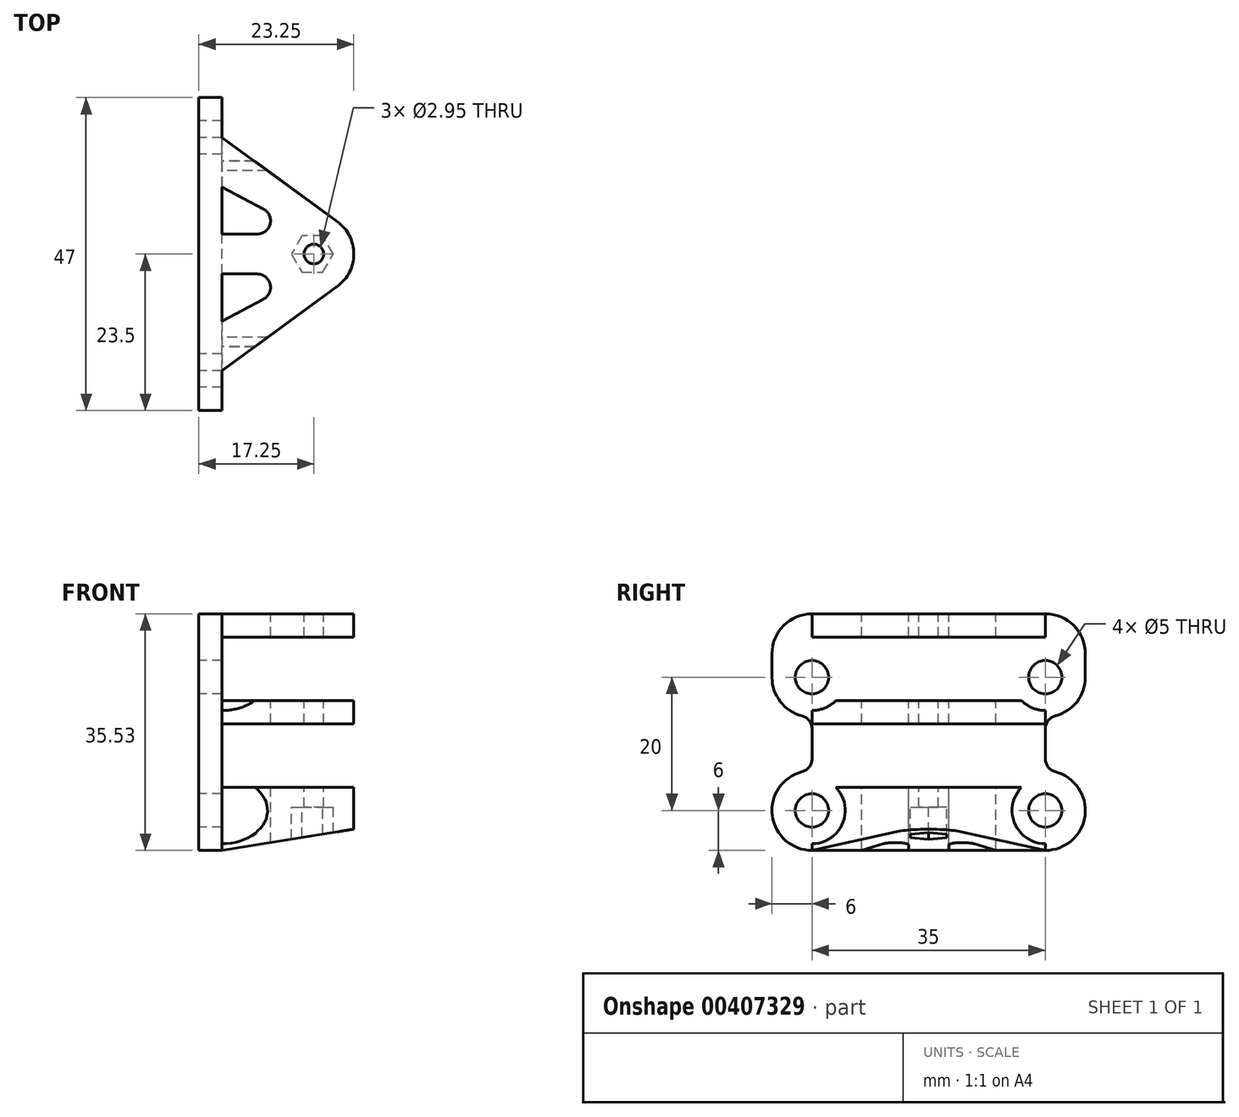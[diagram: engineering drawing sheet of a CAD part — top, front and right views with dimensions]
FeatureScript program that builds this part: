
annotation { "Feature Type Name" : "Feature", "Feature Type Description" : "" }
export const myFeature = defineFeature(function(context is Context, id is Id, definition is map)
    precondition{}
    {
        {
            var Q0;
            Q0=qCreatedBy(makeId("Right.planeOp"),FACE);
            var sketch = newSketch(context, id + "F0", { "sketchPlane" : qUnion([Q0])});
            skLineSegment(sketch, "E0", {"start": v(0, 0) * mm, "end": v(136.08, 0) * mm, "construction": true});
            skLineSegment(sketch, "E1", {"start": v(0, -20) * mm, "end": v(136.08, -20) * mm, "construction": true});
            skLineSegment(sketch, "E2.MirrorCS", {"start": v(0, 20) * mm, "end": v(136.08, 20) * mm, "construction": true});
            skLineSegment(sketch, "E3", {"start": v(0, 20) * mm, "end": v(0, -20) * mm, "construction": true});
            skLineSegment(sketch, "E4", {"start": v(0, -10) * mm, "end": v(136.08, -10) * mm, "construction": true});
            skLineSegment(sketch, "E5.MirrorCS", {"start": v(0, 10) * mm, "end": v(136.08, 10) * mm, "construction": true});
            skLineSegment(sketch, "E6", {"start": v(0, -13.1) * mm, "end": v(136.08, -13.1) * mm, "construction": true});
            skLineSegment(sketch, "E7.MirrorCS", {"start": v(0, -6.9) * mm, "end": v(136.08, -6.9) * mm, "construction": true});
            skLineSegment(sketch, "E8.MirrorCS", {"start": v(0, 6.9) * mm, "end": v(136.08, 6.9) * mm, "construction": true});
            skLineSegment(sketch, "E9.MirrorCS", {"start": v(0, 13.1) * mm, "end": v(136.08, 13.1) * mm, "construction": true});
            skCircle(sketch, "E10", {"center": v(78.97, -10) * mm, "radius": 8 * mm});
            skCircle(sketch, "E11", {"center": v(101.3, 2.1) * mm, "radius": 8 * mm});
            skCircle(sketch, "E12.0", {"center": v(78.97, -10) * mm, "radius": 9.4 * mm});
            skCircle(sketch, "E13.0", {"center": v(101.3, 2.1) * mm, "radius": 9.4 * mm});
            skLineSegment(sketch, "E14", {"start": v(78.97, -1.75) * mm, "end": v(13.68, -1.75) * mm, "construction": true});
            skArc(sketch, "E15", {"start": v(87.21, -10.39) * mm, "mid": v(84.94, -4.3) * mm, "end": v(78.97, -1.75) * mm, "construction": true});
            skLineSegment(sketch, "E16", {"start": v(101.3, 11.25) * mm, "end": v(11.45, 11.25) * mm, "construction": true});
            skArc(sketch, "E17", {"start": v(101.3, 11.25) * mm, "mid": v(108.42, 7.84) * mm, "end": v(110.23, 0.16) * mm, "construction": true});
            skLineSegment(sketch, "E18", {"start": v(22, 11.25) * mm, "end": v(22, -1.75) * mm, "construction": true});
            skLineSegment(sketch, "E19", {"start": v(29.5, -1.75) * mm, "end": v(29.5, 11.25) * mm, "construction": true});
            skLineSegment(sketch, "E20", {"start": v(25.75, -1.75) * mm, "end": v(25.75, 11.25) * mm, "construction": true});
            skLineSegment(sketch, "E21", {"start": v(26, -4.75) * mm, "end": v(26, 1.25) * mm, "construction": true});
            skLineSegment(sketch, "E22", {"start": v(26, 1.25) * mm, "end": v(36, 1.25) * mm, "construction": true});
            skLineSegment(sketch, "E23", {"start": v(36, 1.25) * mm, "end": v(36, -4.75) * mm, "construction": true});
            skLineSegment(sketch, "E24", {"start": v(36, -4.75) * mm, "end": v(26, -4.75) * mm, "construction": true});
            skLineSegment(sketch, "E25.bottom", {"start": v(26, 14.25) * mm, "end": v(36, 14.25) * mm, "construction": true});
            skLineSegment(sketch, "E25.top", {"start": v(26, 8.25) * mm, "end": v(36, 8.25) * mm, "construction": true});
            skLineSegment(sketch, "E25.left", {"start": v(26, 14.25) * mm, "end": v(26, 8.25) * mm, "construction": true});
            skLineSegment(sketch, "E25.right", {"start": v(36, 14.25) * mm, "end": v(36, 8.25) * mm, "construction": true});
            skLineSegment(sketch, "E26.bottom", {"start": v(54.5, -16) * mm, "end": v(7.5, -16) * mm});
            skLineSegment(sketch, "E26.top", {"start": v(54.5, 19.52) * mm, "end": v(7.5, 19.52) * mm});
            skLineSegment(sketch, "E26.left", {"start": v(54.5, -16) * mm, "end": v(54.5, 19.52) * mm});
            skLineSegment(sketch, "E26.right", {"start": v(7.5, -16) * mm, "end": v(7.5, 19.52) * mm});
            skCircle(sketch, "E27", {"center": v(48.5, -10) * mm, "radius": 2.5 * mm});
            skCircle(sketch, "E28", {"center": v(13.5, -10) * mm, "radius": 2.5 * mm});
            skCircle(sketch, "E29", {"center": v(13.5, -10) * mm, "radius": 5 * mm});
            skCircle(sketch, "E30", {"center": v(48.5, -10) * mm, "radius": 5 * mm});
            skCircle(sketch, "E31", {"center": v(48.5, 10) * mm, "radius": 2.5 * mm});
            skCircle(sketch, "E32", {"center": v(48.5, 10) * mm, "radius": 5 * mm});
            skCircle(sketch, "E33", {"center": v(13.5, 10) * mm, "radius": 2.5 * mm});
            skCircle(sketch, "E34", {"center": v(13.5, 10) * mm, "radius": 5 * mm});
            skLineSegment(sketch, "E35", {"start": v(48.5, -10) * mm, "end": v(48.5, 10) * mm, "construction": true});
            skLineSegment(sketch, "E36", {"start": v(13.5, -10) * mm, "end": v(13.5, 10) * mm, "construction": true});
            skLineSegment(sketch, "E37", {"start": v(34.42, 8.25) * mm, "end": v(34.42, 6.47) * mm, "construction": true});
            skLineSegment(sketch, "E38", {"start": v(34.42, 6.47) * mm, "end": v(27.58, 6.47) * mm});
            skLineSegment(sketch, "E39", {"start": v(27.58, 6.47) * mm, "end": v(27.58, 8.25) * mm, "construction": true});
            skLineSegment(sketch, "E40", {"start": v(31, 20.34) * mm, "end": v(31, -14.66) * mm, "construction": true});
            skLineSegment(sketch, "E41", {"start": v(34.42, 14.25) * mm, "end": v(34.42, 16.02) * mm, "construction": true});
            skLineSegment(sketch, "E42", {"start": v(34.42, 16.02) * mm, "end": v(27.58, 16.02) * mm, "construction": true});
            skLineSegment(sketch, "E43", {"start": v(27.58, 16.02) * mm, "end": v(27.58, 14.25) * mm, "construction": true});
            skLineSegment(sketch, "E44", {"start": v(34.42, -4.75) * mm, "end": v(34.42, -6.53) * mm, "construction": true});
            skLineSegment(sketch, "E45", {"start": v(34.42, -6.53) * mm, "end": v(27.58, -6.53) * mm, "construction": true});
            skLineSegment(sketch, "E46", {"start": v(27.58, -6.53) * mm, "end": v(27.58, -4.75) * mm, "construction": true});
            skLineSegment(sketch, "E47", {"start": v(34.42, 1.25) * mm, "end": v(34.42, 3.02) * mm, "construction": true});
            skLineSegment(sketch, "E48", {"start": v(34.42, 3.02) * mm, "end": v(27.58, 3.02) * mm, "construction": true});
            skLineSegment(sketch, "E49", {"start": v(27.58, 3.02) * mm, "end": v(27.58, 1.25) * mm, "construction": true});
            skLineSegment(sketch, "E50.bottom", {"start": v(48.5, 16.02) * mm, "end": v(13.5, 16.02) * mm});
            skLineSegment(sketch, "E50.top", {"start": v(48.5, 19.52) * mm, "end": v(13.5, 19.52) * mm});
            skLineSegment(sketch, "E50.left", {"start": v(48.5, 16.02) * mm, "end": v(48.5, 19.52) * mm});
            skLineSegment(sketch, "E50.right", {"start": v(13.5, 16.02) * mm, "end": v(13.5, 19.52) * mm});
            skLineSegment(sketch, "E51.bottom", {"start": v(48.5, 3.02) * mm, "end": v(13.5, 3.02) * mm});
            skLineSegment(sketch, "E51.top", {"start": v(48.5, 6.47) * mm, "end": v(13.5, 6.47) * mm});
            skLineSegment(sketch, "E51.left", {"start": v(48.5, 3.02) * mm, "end": v(48.5, 6.47) * mm});
            skLineSegment(sketch, "E51.right", {"start": v(13.5, 3.02) * mm, "end": v(13.5, 6.47) * mm});
            skLineSegment(sketch, "E52.bottom", {"start": v(48.5, -14.03) * mm, "end": v(13.5, -14.03) * mm});
            skLineSegment(sketch, "E52.top", {"start": v(48.5, -6.53) * mm, "end": v(13.5, -6.53) * mm});
            skLineSegment(sketch, "E52.left", {"start": v(48.5, -14.03) * mm, "end": v(48.5, -6.53) * mm});
            skLineSegment(sketch, "E52.right", {"start": v(13.5, -14.03) * mm, "end": v(13.5, -6.53) * mm});
            skLineSegment(sketch, "E53", {"start": v(32.45, 20.34) * mm, "end": v(32.45, -14.66) * mm, "construction": true});
            skLineSegment(sketch, "E54", {"start": v(32.45, -14.66) * mm, "end": v(29.55, -14.66) * mm, "construction": true});
            skLineSegment(sketch, "E55", {"start": v(29.55, -14.66) * mm, "end": v(29.55, 20.34) * mm, "construction": true});
            skLineSegment(sketch, "E56", {"start": v(29.55, 20.34) * mm, "end": v(32.45, 20.34) * mm});
            skLineSegment(sketch, "E57.bottom", {"start": v(35.4, 19.52) * mm, "end": v(26.6, 19.52) * mm});
            skLineSegment(sketch, "E57.top", {"start": v(35.4, 20.34) * mm, "end": v(26.6, 20.34) * mm});
            skLineSegment(sketch, "E57.left", {"start": v(35.4, 19.52) * mm, "end": v(35.4, 20.34) * mm});
            skLineSegment(sketch, "E57.right", {"start": v(26.6, 19.52) * mm, "end": v(26.6, 20.34) * mm});
            skLineSegment(sketch, "E58", {"start": v(33.75, -14.03) * mm, "end": v(33.75, -10.03) * mm});
            skLineSegment(sketch, "E59", {"start": v(33.75, -10.03) * mm, "end": v(28.25, -10.03) * mm});
            skLineSegment(sketch, "E60", {"start": v(28.25, -10.03) * mm, "end": v(28.25, -14.03) * mm});
            skLineSegment(sketch, "E61", {"start": v(48.5, -14.03) * mm, "end": v(48.5, -16) * mm});
            skLineSegment(sketch, "E62", {"start": v(13.5, -14.03) * mm, "end": v(13.5, -16) * mm});
            skArc(sketch, "E63", {"start": v(48.5, -16) * mm, "mid": v(54.45, -10.76) * mm, "end": v(50, -4.2) * mm});
            skArc(sketch, "E64", {"start": v(48.5, 19.52) * mm, "mid": v(52.74, 17.77) * mm, "end": v(54.5, 13.52) * mm});
            skLineSegment(sketch, "E65", {"start": v(48.5, 2.25) * mm, "end": v(48.5, -2.25) * mm});
            skArc(sketch, "E66", {"start": v(54.5, 10) * mm, "mid": v(53.24, 6.33) * mm, "end": v(50, 4.2) * mm});
            skPoint(sketch, "E67.visualSharp", {"position": v(48.5, -4) * mm});
            skArc(sketch, "E67.filletArc", {"start": v(48.5, -2.25) * mm, "mid": v(48.92, -3.48) * mm, "end": v(50, -4.2) * mm});
            skPoint(sketch, "E68.visualSharp", {"position": v(48.5, 4) * mm});
            skArc(sketch, "E68.filletArc", {"start": v(50, 4.2) * mm, "mid": v(48.92, 3.48) * mm, "end": v(48.5, 2.25) * mm});
            skArc(sketch, "E69.MirrorCS", {"start": v(13.5, -16) * mm, "mid": v(7.55, -10.76) * mm, "end": v(12, -4.2) * mm});
            skArc(sketch, "E70.MirrorCS", {"start": v(13.5, -2.25) * mm, "mid": v(13.08, -3.48) * mm, "end": v(12, -4.2) * mm});
            skArc(sketch, "E71.MirrorCS", {"start": v(12, 4.2) * mm, "mid": v(13.08, 3.48) * mm, "end": v(13.5, 2.25) * mm});
            skArc(sketch, "E72.MirrorCS", {"start": v(7.5, 10) * mm, "mid": v(8.76, 6.33) * mm, "end": v(12, 4.2) * mm});
            skArc(sketch, "E73.MirrorCS", {"start": v(13.5, 19.52) * mm, "mid": v(9.26, 17.77) * mm, "end": v(7.5, 13.52) * mm});
            skLineSegment(sketch, "E74.MirrorCS", {"start": v(13.5, 2.25) * mm, "end": v(13.5, -2.25) * mm});
            skSolve(sketch);
        }
        {
            var Q0;
            {var subQ0=sQuery(id+"F0.wireOp",EDGE,"E52.left");var subQ8=sQuery(id+"F0.wireOp",EDGE,"E27");var subQ9=makeQuery(id+"F0.imprint","INTERSECT",VERTEX,{"disambiguationData":[OD(0.0)],"derivedFrom":[subQ8,subQ0]});Q0=makeQuery(id+"F0.imprint","IMPRINT",FACE,{"disambiguationData":[TD([[makeQuery(id+"F0.imprint","IMPRINT",EDGE,{"disambiguationData":[TD([[subQ9,1.0]])],"derivedFrom":subQ8}),-1.0]])]});}
            var Q1;
            {var subQ0=sQuery(id+"F0.wireOp",EDGE,"E52.left");var subQ8=sQuery(id+"F0.wireOp",EDGE,"E27");var subQ9=makeQuery(id+"F0.imprint","INTERSECT",VERTEX,{"disambiguationData":[OD(0.0)],"derivedFrom":[subQ8,subQ0]});Q1=makeQuery(id+"F0.imprint","IMPRINT",FACE,{"disambiguationData":[TD([[makeQuery(id+"F0.imprint","IMPRINT",EDGE,{"disambiguationData":[TD([[subQ9,1.0]])],"derivedFrom":subQ8}),-1.0]])]});}
            var Q2;
            {var subQ1=sQuery(id+"F0.wireOp",EDGE,"E52.left");var subQ3=sQuery(id+"F0.wireOp",EDGE,"E27");var subQ4=makeQuery(id+"F0.imprint","INTERSECT",VERTEX,{"disambiguationData":[OD(0.0)],"derivedFrom":[subQ3,subQ1]});Q2=makeQuery(id+"F0.imprint","IMPRINT",FACE,{"disambiguationData":[TD([[makeQuery(id+"F0.imprint","IMPRINT",EDGE,{"disambiguationData":[TD([[subQ4,-1.0]])],"derivedFrom":subQ3}),-1.0]])]});}
            var Q3;
            {var subQ0=sQuery(id+"F0.wireOp",EDGE,"E52.right");var subQ8=sQuery(id+"F0.wireOp",EDGE,"E28");var subQ9=makeQuery(id+"F0.imprint","INTERSECT",VERTEX,{"disambiguationData":[OD(0.0)],"derivedFrom":[subQ8,subQ0]});Q3=makeQuery(id+"F0.imprint","IMPRINT",FACE,{"disambiguationData":[TD([[makeQuery(id+"F0.imprint","IMPRINT",EDGE,{"disambiguationData":[TD([[subQ9,1.0]])],"derivedFrom":subQ8}),-1.0]])]});}
            var Q4;
            {var subQ0=sQuery(id+"F0.wireOp",EDGE,"E52.right");var subQ8=sQuery(id+"F0.wireOp",EDGE,"E28");var subQ9=makeQuery(id+"F0.imprint","INTERSECT",VERTEX,{"disambiguationData":[OD(0.0)],"derivedFrom":[subQ8,subQ0]});Q4=makeQuery(id+"F0.imprint","IMPRINT",FACE,{"disambiguationData":[TD([[makeQuery(id+"F0.imprint","IMPRINT",EDGE,{"disambiguationData":[TD([[subQ9,-1.0]])],"derivedFrom":subQ8}),-1.0]])]});}
            var Q5;
            {var subQ0=sQuery(id+"F0.wireOp",EDGE,"E52.right");var subQ8=sQuery(id+"F0.wireOp",EDGE,"E28");var subQ9=makeQuery(id+"F0.imprint","INTERSECT",VERTEX,{"disambiguationData":[OD(0.0)],"derivedFrom":[subQ8,subQ0]});Q5=makeQuery(id+"F0.imprint","IMPRINT",FACE,{"disambiguationData":[TD([[makeQuery(id+"F0.imprint","IMPRINT",EDGE,{"disambiguationData":[TD([[subQ9,-1.0]])],"derivedFrom":subQ8}),-1.0]])]});}
            var Q6;
            Q6=makeQuery(id+"F0.imprint","IMPRINT",FACE,{"disambiguationData":[TD([[makeQuery(id+"F0.imprint","IMPRINT",EDGE,{"derivedFrom":sQuery(id+"F0.wireOp",EDGE,"E31")}),-1.0]])]});
            var Q7;
            Q7=makeQuery(id+"F0.imprint","IMPRINT",FACE,{"disambiguationData":[TD([[makeQuery(id+"F0.imprint","IMPRINT",EDGE,{"derivedFrom":sQuery(id+"F0.wireOp",EDGE,"E33")}),-1.0]])]});
            var Q8;
            {var subQ0=sQuery(id+"F0.wireOp",EDGE,"E52.bottom");var subQ1=sQuery(id+"F0.wireOp",EDGE,"E30");var subQ2=makeQuery(id+"F0.imprint","INTERSECT",VERTEX,{"derivedFrom":[subQ1,subQ0]});Q8=makeQuery(id+"F0.imprint","IMPRINT",FACE,{"disambiguationData":[TD([[makeQuery(id+"F0.imprint","IMPRINT",EDGE,{"disambiguationData":[TD([[subQ2,-1.0]])],"derivedFrom":subQ1}),1.0]])]});}
            var Q9;
            {var subQ0=sQuery(id+"F0.wireOp",EDGE,"E62");var subQ1=sQuery(id+"F0.wireOp",EDGE,"E29");var subQ2=makeQuery(id+"F0.imprint","INTERSECT",VERTEX,{"derivedFrom":[subQ1,subQ0]});Q9=makeQuery(id+"F0.imprint","IMPRINT",FACE,{"disambiguationData":[TD([[makeQuery(id+"F0.imprint","IMPRINT",EDGE,{"disambiguationData":[TD([[subQ2,-1.0]])],"derivedFrom":subQ1}),1.0]])]});}
            var Q10;
            {var subQ0=sQuery(id+"F0.wireOp",EDGE,"E51.top");var subQ1=sQuery(id+"F0.wireOp",EDGE,"E34");var subQ2=makeQuery(id+"F0.imprint","INTERSECT",VERTEX,{"derivedFrom":[subQ1,subQ0]});Q10=makeQuery(id+"F0.imprint","IMPRINT",FACE,{"disambiguationData":[TD([[makeQuery(id+"F0.imprint","IMPRINT",EDGE,{"disambiguationData":[TD([[subQ2,1.0]])],"derivedFrom":subQ1}),1.0]])]});}
            var Q11;
            {var subQ0=sQuery(id+"F0.wireOp",EDGE,"E51.top");var subQ1=sQuery(id+"F0.wireOp",EDGE,"E32");var subQ2=makeQuery(id+"F0.imprint","INTERSECT",VERTEX,{"derivedFrom":[subQ1,subQ0]});Q11=makeQuery(id+"F0.imprint","IMPRINT",FACE,{"disambiguationData":[TD([[makeQuery(id+"F0.imprint","IMPRINT",EDGE,{"disambiguationData":[TD([[subQ2,-1.0]])],"derivedFrom":subQ1}),1.0]])]});}
            var Q12;
            Q12=makeQuery(id+"F0.imprint","IMPRINT",FACE,{"disambiguationData":[TD([[makeQuery(id+"F0.imprint","IMPRINT",EDGE,{"derivedFrom":sQuery(id+"F0.wireOp",EDGE,"E50.bottom")}),1.0]])]});
            extrude(context, id + "F1", {"entities" : qUnion([Q0, Q1, Q2, Q3, Q4, Q5, Q6, Q7, Q8, Q9, Q10, Q11, Q12]), "depth" : 3.5 * mm});
        }
        {
            var Q0;
            {var subQ0=sQuery(id+"F0.wireOp",EDGE,"E58");Q0=makeQuery(id+"F0.imprint","IMPRINT",FACE,{"disambiguationData":[TD([[makeQuery(id+"F0.imprint","IMPRINT",EDGE,{"derivedFrom":subQ0}),1.0]])]});}
            var Q1;
            {var subQ9=sQuery(id+"F0.wireOp",EDGE,"E51.bottom");Q1=makeQuery(id+"F0.imprint","IMPRINT",FACE,{"disambiguationData":[TD([[makeQuery(id+"F0.imprint","IMPRINT",EDGE,{"derivedFrom":subQ9}),-1.0]])]});}
            var Q2;
            Q2=makeQuery(id+"F0.imprint","IMPRINT",FACE,{"disambiguationData":[TD([[makeQuery(id+"F0.imprint","IMPRINT",EDGE,{"derivedFrom":sQuery(id+"F0.wireOp",EDGE,"E50.bottom")}),-1.0]])]});
            var Q3;
            {var subQ4=sQuery(id+"F0.wireOp",EDGE,"E58");Q3=makeQuery(id+"F0.imprint","IMPRINT",FACE,{"disambiguationData":[TD([[makeQuery(id+"F0.imprint","IMPRINT",EDGE,{"derivedFrom":subQ4}),-1.0]])]});}
            var Q4;
            {var subQ4=sQuery(id+"F0.wireOp",EDGE,"E61");var subQ10=sQuery(id+"F0.wireOp",EDGE,"E26.bottom");var subQ11=makeQuery(id+"F0.imprint","INTERSECT",VERTEX,{"derivedFrom":[subQ10,subQ4]});Q4=makeQuery(id+"F0.imprint","IMPRINT",FACE,{"disambiguationData":[TD([[makeQuery(id+"F0.imprint","IMPRINT",EDGE,{"disambiguationData":[TD([[subQ11,-1.0]])],"derivedFrom":subQ10}),-1.0]])]});}
            extrude(context, id + "F2", {"entities" : qUnion([Q0, Q1, Q2, Q3, Q4]), "operationType" : NewBodyOperationType.ADD, "depth" : 25 * mm});
        }
        {
            var Q0;
            Q0=makeQuery(id+"F1.opExtrude","SWEPT_FACE",FACE,{"disambiguationData":[OSD([sQuery(id+"F0.wireOp",EDGE,"E26.left")])]});
            var sketch = newSketch(context, id + "F3", { "sketchPlane" : qUnion([Q0])});
            skLineSegment(sketch, "E75.0", {"start": v(-25, -6.53) * mm, "end": v(-3.5, -6.53) * mm, "construction": true});
            skLineSegment(sketch, "E76", {"start": v(-25, -16) * mm, "end": v(-25, -12.53) * mm});
            skLineSegment(sketch, "E77", {"start": v(-25, -12.53) * mm, "end": v(-3.5, -16) * mm});
            skLineSegment(sketch, "E78.0", {"start": v(-25, -16) * mm, "end": v(-3.5, -16) * mm});
            skSolve(sketch);
        }
        {
            var Q0;
            Q0=makeQuery(id+"F3.imprint","IMPRINT",FACE,{"disambiguationData":[TD([[makeQuery(id+"F3.imprint","IMPRINT",EDGE,{"derivedFrom":sQuery(id+"F3.wireOp",EDGE,"E76")}),-1.0]])]});
            extrude(context, id + "F4", {"entities" : qUnion([Q0]), "operationType" : NewBodyOperationType.REMOVE, "endBound" : BoundingType.THROUGH_ALL, "oppositeDirection" : true, "depth" : 25 * mm});
        }
        {
            var Q0;
            Q0=qCreatedBy(makeId("Top.planeOp"),FACE);
            var sketch = newSketch(context, id + "F5", { "sketchPlane" : qUnion([Q0])});
            skLineSegment(sketch, "E79", {"start": v(0, 0) * mm, "end": v(0, 97.06) * mm, "construction": true});
            skLineSegment(sketch, "E80", {"start": v(8, 0) * mm, "end": v(8, 95.46) * mm, "construction": true});
            skLineSegment(sketch, "E81", {"start": v(16, 0) * mm, "end": v(16, 97.02) * mm, "construction": true});
            skLineSegment(sketch, "E82", {"start": v(0, 0) * mm, "end": v(24.6, 0) * mm, "construction": true});
            skLineSegment(sketch, "E83", {"start": v(12, 96.15) * mm, "end": v(12, 0) * mm, "construction": true});
            skCircle(sketch, "E84", {"center": v(17.25, 31) * mm, "radius": 5 * mm, "construction": true});
            skCircle(sketch, "E85", {"center": v(17.25, 31) * mm, "radius": 5.72 * mm, "construction": true});
            skLineSegment(sketch, "E86", {"start": v(12.25, 81.16) * mm, "end": v(12.25, 31) * mm, "construction": true});
            skCircle(sketch, "E87", {"center": v(17.25, 31) * mm, "radius": 1.48 * mm});
            skArc(sketch, "E88", {"start": v(20.8, 26.16) * mm, "mid": v(23.25, 31) * mm, "end": v(20.8, 35.84) * mm});
            skLineSegment(sketch, "E89", {"start": v(20.8, 35.84) * mm, "end": v(3.5, 48.5) * mm});
            skLineSegment(sketch, "E90", {"start": v(20.8, 26.16) * mm, "end": v(3.5, 13.5) * mm});
            skLineSegment(sketch, "E91", {"start": v(3.5, 31) * mm, "end": v(25, 31) * mm, "construction": true});
            skLineSegment(sketch, "E92", {"start": v(25, 13.5) * mm, "end": v(25, 48.5) * mm});
            skLineSegment(sketch, "E93", {"start": v(3.5, 20.94) * mm, "end": v(9.7, 24.23) * mm});
            skLineSegment(sketch, "E94", {"start": v(8.76, 28) * mm, "end": v(3.5, 28) * mm});
            skPoint(sketch, "E95", {"position": v(3.5, 30.45) * mm});
            skLineSegment(sketch, "E96.MirrorCS", {"start": v(8.76, 34) * mm, "end": v(3.5, 34) * mm});
            skLineSegment(sketch, "E97.MirrorCS", {"start": v(3.5, 41.06) * mm, "end": v(9.7, 37.77) * mm});
            skPoint(sketch, "E98.visualSharp", {"position": v(16.78, 34) * mm});
            skArc(sketch, "E98.filletArc", {"start": v(8.76, 34) * mm, "mid": v(10.7, 35.52) * mm, "end": v(9.7, 37.77) * mm});
            skPoint(sketch, "E99.visualSharp", {"position": v(16.78, 28) * mm});
            skArc(sketch, "E99.filletArc", {"start": v(9.7, 24.23) * mm, "mid": v(10.7, 26.48) * mm, "end": v(8.76, 28) * mm});
            skLineSegment(sketch, "E100.0", {"start": v(25, 13.5) * mm, "end": v(3.5, 13.5) * mm});
            skLineSegment(sketch, "E100.1", {"start": v(25, 48.5) * mm, "end": v(3.5, 48.5) * mm});
            skLineSegment(sketch, "E101.0", {"start": v(3.5, 48.5) * mm, "end": v(3.5, 13.5) * mm});
            skSolve(sketch);
        }
        {
            var Q0;
            Q0=makeQuery(id+"F5.imprint","IMPRINT",FACE,{"disambiguationData":[TD([[makeQuery(id+"F5.imprint","IMPRINT",EDGE,{"derivedFrom":sQuery(id+"F5.wireOp",EDGE,"E88")}),-1.0]])]});
            var Q1;
            Q1=makeQuery(id+"F5.imprint","IMPRINT",FACE,{"disambiguationData":[TD([[makeQuery(id+"F5.imprint","IMPRINT",EDGE,{"derivedFrom":sQuery(id+"F5.wireOp",EDGE,"E87")}),1.0]])]});
            var Q2;
            {var subQ0=sQuery(id+"F5.wireOp",EDGE,"E96.MirrorCS");Q2=makeQuery(id+"F5.imprint","IMPRINT",FACE,{"disambiguationData":[TD([[makeQuery(id+"F5.imprint","IMPRINT",EDGE,{"derivedFrom":subQ0}),-1.0]])]});}
            var Q3;
            {var subQ0=sQuery(id+"F5.wireOp",EDGE,"E93");Q3=makeQuery(id+"F5.imprint","IMPRINT",FACE,{"disambiguationData":[TD([[makeQuery(id+"F5.imprint","IMPRINT",EDGE,{"derivedFrom":subQ0}),1.0]])]});}
            var Q4;
            Q4=sQuery(id+"F5.wireOp",EDGE,"E86");
            extrude(context, id + "F6", {"entities" : qUnion([Q0, Q1, Q2, Q3]), "operationType" : NewBodyOperationType.REMOVE, "surfaceEntities" : qUnion([Q4]), "endBound" : BoundingType.THROUGH_ALL, "oppositeDirection" : true, "depth" : 25 * mm, "hasSecondDirection" : true, "secondDirectionBound" : SecondDirectionBoundingType.THROUGH_ALL, "secondDirectionOppositeDirection" : false, "secondDirectionDepth" : 25 * mm});
        }
        {
            var Q0;
            Q0=makeQuery(id+"F2.opExtrude","SWEPT_FACE",FACE,{"disambiguationData":[OSD([sQuery(id+"F0.wireOp",EDGE,"E52.top")])]});
            cPlane(context, id + "F7", {"entities" : qUnion([Q0]), "cplaneType" : CPlaneType.OFFSET, "offset" : 3 * mm, "oppositeDirection" : true, "width" : 150 * mm, "height" : 150 * mm});
        }
        {
            var Q0;
            Q0=qCreatedBy(id+"F7.planeOp",FACE);
            var sketch = newSketch(context, id + "F8", { "sketchPlane" : qUnion([Q0])});
            skCircle(sketch, "E102.0", {"center": v(17.25, 31) * mm, "radius": 1.48 * mm});
            skCircle(sketch, "E103.cCircle", {"center": v(17.03, 31) * mm, "radius": 2.72 * mm, "construction": true});
            skLineSegment(sketch, "E103.0", {"start": v(18.6, 33.73) * mm, "end": v(20.17, 31) * mm});
            skLineSegment(sketch, "E103.1", {"start": v(20.17, 31) * mm, "end": v(18.6, 28.27) * mm});
            skLineSegment(sketch, "E103.2", {"start": v(18.6, 28.28) * mm, "end": v(15.45, 28.28) * mm});
            skLineSegment(sketch, "E103.3", {"start": v(15.45, 28.27) * mm, "end": v(13.88, 31) * mm});
            skLineSegment(sketch, "E103.4", {"start": v(13.88, 31) * mm, "end": v(15.45, 33.72) * mm});
            skLineSegment(sketch, "E103.5", {"start": v(15.45, 33.72) * mm, "end": v(18.6, 33.72) * mm});
            skPoint(sketch, "E103.0.midPoint", {"position": v(19.39, 32.36) * mm});
            skSolve(sketch);
        }
        {
            var Q0;
            Q0=makeQuery(id+"F8.imprint","IMPRINT",FACE,{"disambiguationData":[TD([[makeQuery(id+"F8.imprint","IMPRINT",EDGE,{"derivedFrom":sQuery(id+"F8.wireOp",EDGE,"E102.0")}),-1.0]])]});
            extrude(context, id + "F9", {"entities" : qUnion([Q0]), "operationType" : NewBodyOperationType.REMOVE, "endBound" : BoundingType.THROUGH_ALL, "oppositeDirection" : true, "depth" : 25 * mm});
        }
    });
